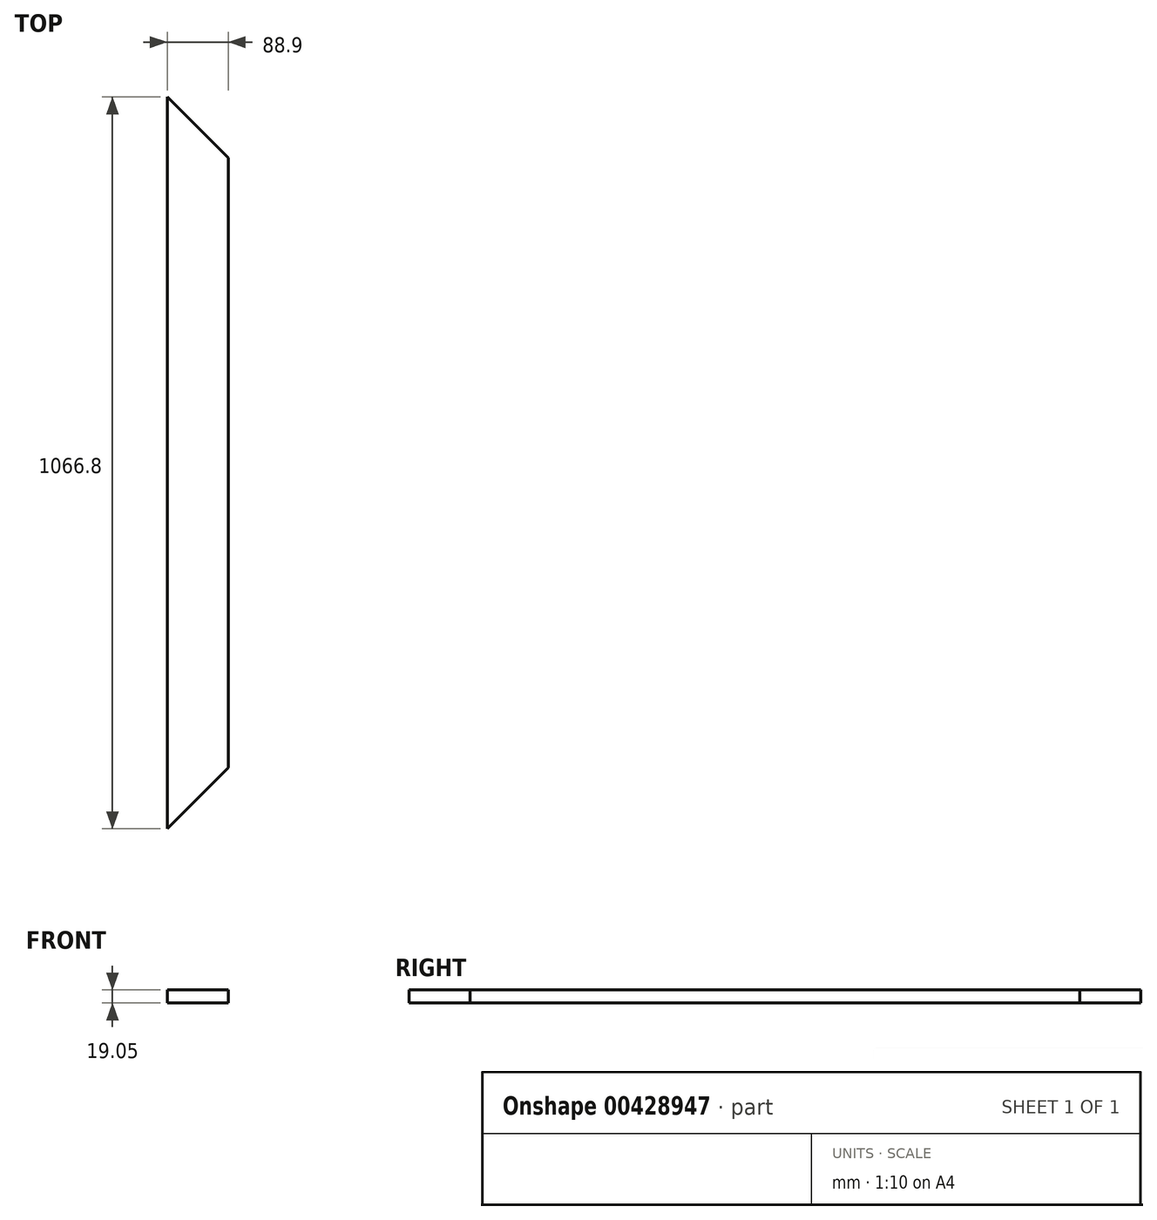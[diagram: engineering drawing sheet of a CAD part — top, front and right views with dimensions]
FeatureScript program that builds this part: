
annotation { "Feature Type Name" : "Feature", "Feature Type Description" : "" }
export const myFeature = defineFeature(function(context is Context, id is Id, definition is map)
    precondition{}
    {
        {
            var Q0;
            Q0=qCreatedBy(makeId("Top.planeOp"),FACE);
            var sketch = newSketch(context, id + "F0", { "sketchPlane" : qUnion([Q0])});
            skLineSegment(sketch, "E0.bottom", {"start": v(-7.96, 1005.36) * mm, "end": v(-96.86, 1005.36) * mm});
            skLineSegment(sketch, "E0.top", {"start": v(-7.96, -61.44) * mm, "end": v(-96.86, -61.44) * mm});
            skLineSegment(sketch, "E0.left", {"start": v(-7.96, 1005.36) * mm, "end": v(-7.96, -61.44) * mm});
            skLineSegment(sketch, "E0.right", {"start": v(-96.86, 1005.36) * mm, "end": v(-96.86, -61.44) * mm});
            skSolve(sketch);
        }
        {
            var Q0;
            Q0=makeQuery(id+"F0.imprint","IMPRINT",FACE,{"disambiguationData":[TD([[makeQuery(id+"F0.imprint","IMPRINT",EDGE,{"derivedFrom":sQuery(id+"F0.wireOp",EDGE,"E0.bottom")}),1.0]])]});
            extrude(context, id + "F1", {"entities" : qUnion([Q0]), "depth" : 19.05 * mm});
        }
        {
            var Q0;
            Q0=makeQuery(id+"F1.opExtrude","SWEPT_EDGE",EDGE,{"disambiguationData":[OSD([sQuery(id+"F0.wireOp",EDGE,"E0.top"),sQuery(id+"F0.wireOp",EDGE,"E0.left")])]});
            chamfer(context, id + "F2", {"entities" : qUnion([Q0]), "width" : 88.9 * mm, "tangentPropagation" : true});
        }
        {
            var Q0;
            Q0=makeQuery(id+"F1.opExtrude","SWEPT_EDGE",EDGE,{"disambiguationData":[OSD([sQuery(id+"F0.wireOp",EDGE,"E0.bottom"),sQuery(id+"F0.wireOp",EDGE,"E0.left")])]});
            chamfer(context, id + "F3", {"entities" : qUnion([Q0]), "width" : 88.9 * mm, "tangentPropagation" : true});
        }
    });
